# Revit family: RAUPIANO PLUS Socket Plug
name_source: partatom
category: Pipe Fittings
revit_build: Autodesk Revit MEP 2012 (Build: 20110309_2315(x64)
units: mm (PartAtom-declared; Revit-internal decimal feet)

## types (1)
- Standard
    A1 = 123134-001
    A2 = 121454-001
    A3 = 121464-001
    A4 = 123334-001
    A5 = 121474-001
    A6 = 120624-001
    A7 = 123774-002
    A8 = 123974-001
    Description = REHAU RAUPIANO PLUS socket plug
    Fail = No article found
    Lookup Table Name = RAUPIANO Socket Plug.csv
    Loss Method = Not Defined
    M1 = 11231341001
    M2 = 11231341001
    M3 = 11214641001
    M4 = 11233341001
    M5 = 11214741001
    M6 = 11206241001
    M7 = 11237741002
    M8 = 11239741001
    Manufacturer = REHAU
    T1 = DN 40
    T2 = DN 50
    T3 = DN 75
    T4 = DN 90
    T5 = DN 110
    T6 = DN 125
    T7 = DN 160
    T8 = DN 200
    Type Comments = RAU-PP; Push-fit; White

## geometry (parser evidence)
native form markers: Sweep x1
no freeform markers — native parametric forms only
